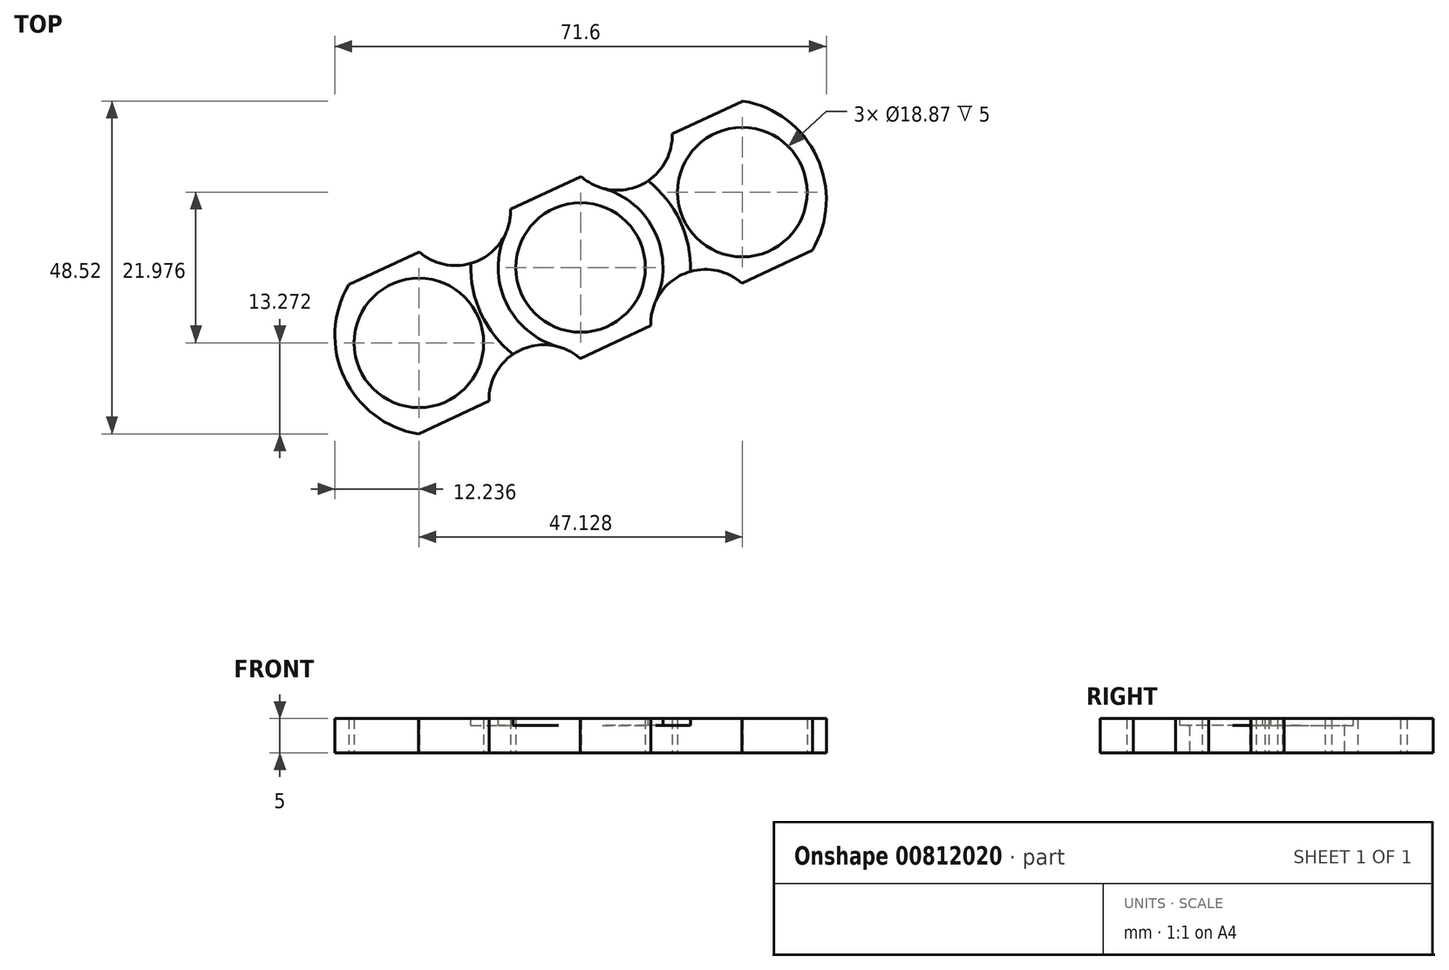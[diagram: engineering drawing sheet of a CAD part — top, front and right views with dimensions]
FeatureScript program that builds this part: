
annotation { "Feature Type Name" : "Feature", "Feature Type Description" : "" }
export const myFeature = defineFeature(function(context is Context, id is Id, definition is map)
    precondition{}
    {
        {
            var Q0;
            Q0=qCreatedBy(makeId("Top.planeOp"),FACE);
            var sketch = newSketch(context, id + "F0", { "sketchPlane" : qUnion([Q0])});
            skCircle(sketch, "E0", {"center": v(0, 0) * mm, "radius": 9.44 * mm});
            skCircle(sketch, "E1", {"center": v(23.56, 10.99) * mm, "radius": 9.44 * mm});
            skCircle(sketch, "E2", {"center": v(-23.56, -10.99) * mm, "radius": 9.44 * mm});
            skLineSegment(sketch, "E3.bottom", {"start": v(-36.75, 25) * mm, "end": v(36.75, 25) * mm, "construction": true});
            skLineSegment(sketch, "E3.top", {"start": v(-36.75, -25) * mm, "end": v(36.75, -25) * mm, "construction": true});
            skLineSegment(sketch, "E3.left", {"start": v(-36.75, 25) * mm, "end": v(-36.75, -25) * mm, "construction": true});
            skLineSegment(sketch, "E3.right", {"start": v(36.75, 25) * mm, "end": v(36.75, -25) * mm, "construction": true});
            skLineSegment(sketch, "E4", {"start": v(-23.56, -10.99) * mm, "end": v(23.56, 10.99) * mm, "construction": true});
            skLineSegment(sketch, "E5", {"start": v(-5.81, 12.46) * mm, "end": v(6.83, -14.65) * mm, "construction": true});
            skLineSegment(sketch, "E6", {"start": v(-33.77, -2.5) * mm, "end": v(-23.5, 2.28) * mm});
            skLineSegment(sketch, "E7", {"start": v(13.36, 19.47) * mm, "end": v(23.63, 24.26) * mm});
            skLineSegment(sketch, "E8", {"start": v(-10.2, 8.48) * mm, "end": v(0.06, 13.27) * mm});
            skLineSegment(sketch, "E9", {"start": v(23.5, -2.28) * mm, "end": v(33.77, 2.5) * mm});
            skLineSegment(sketch, "E10", {"start": v(-23.63, -24.26) * mm, "end": v(-13.36, -19.47) * mm});
            skLineSegment(sketch, "E11", {"start": v(-0.06, -13.27) * mm, "end": v(10.2, -8.48) * mm});
            skArc(sketch, "E12", {"start": v(-33.77, -2.5) * mm, "mid": v(-34.44, -16.06) * mm, "end": v(-23.63, -24.26) * mm});
            skArc(sketch, "E13", {"start": v(33.77, 2.5) * mm, "mid": v(34.44, 16.06) * mm, "end": v(23.63, 24.26) * mm});
            skArc(sketch, "E14", {"start": v(0.06, 13.27) * mm, "mid": v(8.74, 12.02) * mm, "end": v(13.36, 19.47) * mm});
            skArc(sketch, "E15", {"start": v(23.5, -2.28) * mm, "mid": v(14.82, -1.03) * mm, "end": v(10.2, -8.48) * mm});
            skArc(sketch, "E16", {"start": v(-0.06, -13.27) * mm, "mid": v(-8.74, -12.02) * mm, "end": v(-13.36, -19.47) * mm});
            skArc(sketch, "E17", {"start": v(-23.5, 2.28) * mm, "mid": v(-14.82, 1.03) * mm, "end": v(-10.2, 8.48) * mm});
            skLineSegment(sketch, "E18", {"start": v(-23.56, -10.99) * mm, "end": v(-31.51, 6.06) * mm, "construction": true});
            skLineSegment(sketch, "E19", {"start": v(23.56, 10.99) * mm, "end": v(14.6, 30.23) * mm, "construction": true});
            skCircle(sketch, "E20", {"center": v(-23.56, -10.99) * mm, "radius": 12 * mm, "construction": true});
            skCircle(sketch, "E21", {"center": v(0, 0) * mm, "radius": 12 * mm, "construction": true});
            skCircle(sketch, "E22", {"center": v(23.56, 10.99) * mm, "radius": 12 * mm, "construction": true});
            skSolve(sketch);
        }
        {
            var Q0;
            Q0=makeQuery(id+"F0.imprint","IMPRINT",FACE,{"disambiguationData":[TD([[makeQuery(id+"F0.imprint","IMPRINT",EDGE,{"derivedFrom":sQuery(id+"F0.wireOp",EDGE,"E0")}),-1.0]])]});
            extrude(context, id + "F1", {"entities" : qUnion([Q0]), "depth" : 2.5 * mm, "offsetDistance" : 25 * mm, "hasSecondDirection" : true, "secondDirectionOppositeDirection" : true, "secondDirectionDepth" : 2.5 * mm});
        }
        {
            var Q0;
            Q0=makeQuery(id+"F1.opExtrude","CAP_FACE",FACE,{"disambiguationData":[OSD([sQuery(id+"F0.wireOp",EDGE,"E0"),sQuery(id+"F0.wireOp",EDGE,"E1"),sQuery(id+"F0.wireOp",EDGE,"E2"),sQuery(id+"F0.wireOp",EDGE,"E6"),sQuery(id+"F0.wireOp",EDGE,"E7"),sQuery(id+"F0.wireOp",EDGE,"E8"),sQuery(id+"F0.wireOp",EDGE,"E9"),sQuery(id+"F0.wireOp",EDGE,"E10"),sQuery(id+"F0.wireOp",EDGE,"E11"),sQuery(id+"F0.wireOp",EDGE,"E12"),sQuery(id+"F0.wireOp",EDGE,"E13"),sQuery(id+"F0.wireOp",EDGE,"E14"),sQuery(id+"F0.wireOp",EDGE,"E15"),sQuery(id+"F0.wireOp",EDGE,"E16"),sQuery(id+"F0.wireOp",EDGE,"E17")])],"isStart":false});
            var sketch = newSketch(context, id + "F2", { "sketchPlane" : qUnion([Q0])});
            skCircle(sketch, "E23", {"center": v(0, 0) * mm, "radius": 12 * mm});
            skCircle(sketch, "E24", {"center": v(0, 0) * mm, "radius": 16 * mm});
            skSolve(sketch);
        }
        {
            var Q0;
            Q0=makeQuery(id+"F2.imprint","IMPRINT",FACE,{"disambiguationData":[TD([[makeQuery(id+"F2.imprint","IMPRINT",EDGE,{"derivedFrom":makeQuery(id+"F1.opExtrude","CAP_EDGE",EDGE,{"disambiguationData":[OSD([sQuery(id+"F0.wireOp",EDGE,"E0")])],"isStart":false})}),1.0]])]});
            var Q1;
            Q1=makeQuery(id+"F2.imprint","IMPRINT",FACE,{"disambiguationData":[TD([[makeQuery(id+"F2.imprint","IMPRINT",EDGE,{"derivedFrom":makeQuery(id+"F1.opExtrude","CAP_EDGE",EDGE,{"disambiguationData":[OSD([sQuery(id+"F0.wireOp",EDGE,"E1")])],"isStart":false})}),1.0]])]});
            var Q2;
            Q2=makeQuery(id+"F2.imprint","IMPRINT",FACE,{"disambiguationData":[TD([[makeQuery(id+"F2.imprint","IMPRINT",EDGE,{"derivedFrom":makeQuery(id+"F1.opExtrude","CAP_EDGE",EDGE,{"disambiguationData":[OSD([sQuery(id+"F0.wireOp",EDGE,"E2")])],"isStart":false})}),1.0]])]});
            var Q3;
            {var subQ0=sQuery(id+"F2.wireOp",EDGE,"FtA3bayP-j3OT-VSZs-aEoY-GLu4wzKhFJMj");var subQ1=makeQuery(id+"F1.opExtrude","CAP_EDGE",EDGE,{"disambiguationData":[OSD([sQuery(id+"F0.wireOp",EDGE,"E6")])],"isStart":false});var subQ2=makeQuery(id+"F2.imprint","INTERSECT",VERTEX,{"derivedFrom":[subQ1,subQ0]});Q3=makeQuery(id+"F2.imprint","IMPRINT",FACE,{"disambiguationData":[TD([[makeQuery(id+"F2.imprint","IMPRINT",EDGE,{"disambiguationData":[TD([[subQ2,1.0]])],"derivedFrom":subQ0}),-1.0]])]});}
            var Q4;
            {var subQ0=sQuery(id+"F2.wireOp",EDGE,"E23");var subQ1=makeQuery(id+"F1.opExtrude","CAP_EDGE",EDGE,{"disambiguationData":[OSD([sQuery(id+"F0.wireOp",EDGE,"E17")])],"isStart":false});var subQ2=makeQuery(id+"F2.imprint","INTERSECT",VERTEX,{"derivedFrom":[subQ1,subQ0]});Q4=makeQuery(id+"F2.imprint","IMPRINT",FACE,{"disambiguationData":[TD([[makeQuery(id+"F2.imprint","IMPRINT",EDGE,{"disambiguationData":[TD([[subQ2,-1.0]])],"derivedFrom":subQ0}),-1.0]])]});}
            var Q5;
            {var subQ0=sQuery(id+"F2.wireOp",EDGE,"t8nWiPke-CIwg-3ZqW-WhvU-Z3H4iyrQB45r");var subQ1=makeQuery(id+"F1.opExtrude","CAP_EDGE",EDGE,{"disambiguationData":[OSD([sQuery(id+"F0.wireOp",EDGE,"E14")])],"isStart":false});var subQ2=makeQuery(id+"F2.imprint","INTERSECT",VERTEX,{"derivedFrom":[subQ1,subQ0]});Q5=makeQuery(id+"F2.imprint","IMPRINT",FACE,{"disambiguationData":[TD([[makeQuery(id+"F2.imprint","IMPRINT",EDGE,{"disambiguationData":[TD([[subQ2,-1.0]])],"derivedFrom":subQ0}),-1.0]])]});}
            var Q6;
            {var subQ0=sQuery(id+"F2.wireOp",EDGE,"t8nWiPke-CIwg-3ZqW-WhvU-Z3H4iyrQB45r");var subQ1=makeQuery(id+"F1.opExtrude","CAP_EDGE",EDGE,{"disambiguationData":[OSD([sQuery(id+"F0.wireOp",EDGE,"E15")])],"isStart":false});var subQ2=makeQuery(id+"F2.imprint","INTERSECT",VERTEX,{"derivedFrom":[subQ1,subQ0]});Q6=makeQuery(id+"F2.imprint","IMPRINT",FACE,{"disambiguationData":[TD([[makeQuery(id+"F2.imprint","IMPRINT",EDGE,{"disambiguationData":[TD([[subQ2,-1.0]])],"derivedFrom":subQ0}),-1.0]])]});}
            var Q7;
            {var subQ0=sQuery(id+"F2.wireOp",EDGE,"t8nWiPke-CIwg-3ZqW-WhvU-Z3H4iyrQB45r");var subQ1=makeQuery(id+"F1.opExtrude","CAP_EDGE",EDGE,{"disambiguationData":[OSD([sQuery(id+"F0.wireOp",EDGE,"E13")])],"isStart":false});var subQ2=makeQuery(id+"F2.imprint","INTERSECT",VERTEX,{"derivedFrom":[subQ1,subQ0]});Q7=makeQuery(id+"F2.imprint","IMPRINT",FACE,{"disambiguationData":[TD([[makeQuery(id+"F2.imprint","IMPRINT",EDGE,{"disambiguationData":[TD([[subQ2,1.0]])],"derivedFrom":subQ0}),-1.0]])]});}
            var Q8;
            {var subQ0=sQuery(id+"F2.wireOp",EDGE,"t8nWiPke-CIwg-3ZqW-WhvU-Z3H4iyrQB45r");var subQ1=makeQuery(id+"F1.opExtrude","CAP_EDGE",EDGE,{"disambiguationData":[OSD([sQuery(id+"F0.wireOp",EDGE,"E7")])],"isStart":false});var subQ2=makeQuery(id+"F2.imprint","INTERSECT",VERTEX,{"derivedFrom":[subQ1,subQ0]});Q8=makeQuery(id+"F2.imprint","IMPRINT",FACE,{"disambiguationData":[TD([[makeQuery(id+"F2.imprint","IMPRINT",EDGE,{"disambiguationData":[TD([[subQ2,1.0]])],"derivedFrom":subQ0}),-1.0]])]});}
            var Q9;
            {var subQ0=sQuery(id+"F2.wireOp",EDGE,"t8nWiPke-CIwg-3ZqW-WhvU-Z3H4iyrQB45r");var subQ1=makeQuery(id+"F1.opExtrude","CAP_EDGE",EDGE,{"disambiguationData":[OSD([sQuery(id+"F0.wireOp",EDGE,"E7")])],"isStart":false});var subQ2=makeQuery(id+"F2.imprint","INTERSECT",VERTEX,{"derivedFrom":[subQ1,subQ0]});Q9=makeQuery(id+"F2.imprint","IMPRINT",FACE,{"disambiguationData":[TD([[makeQuery(id+"F2.imprint","IMPRINT",EDGE,{"disambiguationData":[TD([[subQ2,-1.0]])],"derivedFrom":subQ0}),-1.0]])]});}
            var Q10;
            {var subQ0=sQuery(id+"F2.wireOp",EDGE,"FtA3bayP-j3OT-VSZs-aEoY-GLu4wzKhFJMj");var subQ1=makeQuery(id+"F1.opExtrude","CAP_EDGE",EDGE,{"disambiguationData":[OSD([sQuery(id+"F0.wireOp",EDGE,"E6")])],"isStart":false});var subQ2=makeQuery(id+"F2.imprint","INTERSECT",VERTEX,{"derivedFrom":[subQ1,subQ0]});Q10=makeQuery(id+"F2.imprint","IMPRINT",FACE,{"disambiguationData":[TD([[makeQuery(id+"F2.imprint","IMPRINT",EDGE,{"disambiguationData":[TD([[subQ2,-1.0]])],"derivedFrom":subQ0}),-1.0]])]});}
            var Q11;
            {var subQ0=sQuery(id+"F2.wireOp",EDGE,"FtA3bayP-j3OT-VSZs-aEoY-GLu4wzKhFJMj");var subQ1=makeQuery(id+"F1.opExtrude","CAP_EDGE",EDGE,{"disambiguationData":[OSD([sQuery(id+"F0.wireOp",EDGE,"E12")])],"isStart":false});var subQ2=makeQuery(id+"F2.imprint","INTERSECT",VERTEX,{"derivedFrom":[subQ1,subQ0]});Q11=makeQuery(id+"F2.imprint","IMPRINT",FACE,{"disambiguationData":[TD([[makeQuery(id+"F2.imprint","IMPRINT",EDGE,{"disambiguationData":[TD([[subQ2,-1.0]])],"derivedFrom":subQ0}),-1.0]])]});}
            var Q12;
            {var subQ0=sQuery(id+"F2.wireOp",EDGE,"FtA3bayP-j3OT-VSZs-aEoY-GLu4wzKhFJMj");var subQ1=makeQuery(id+"F1.opExtrude","CAP_EDGE",EDGE,{"disambiguationData":[OSD([sQuery(id+"F0.wireOp",EDGE,"E10")])],"isStart":false});var subQ2=makeQuery(id+"F2.imprint","INTERSECT",VERTEX,{"derivedFrom":[subQ1,subQ0]});Q12=makeQuery(id+"F2.imprint","IMPRINT",FACE,{"disambiguationData":[TD([[makeQuery(id+"F2.imprint","IMPRINT",EDGE,{"disambiguationData":[TD([[subQ2,-1.0]])],"derivedFrom":subQ0}),-1.0]])]});}
            var Q13;
            {var subQ0=sQuery(id+"F2.wireOp",EDGE,"E23");var subQ1=makeQuery(id+"F1.opExtrude","CAP_EDGE",EDGE,{"disambiguationData":[OSD([sQuery(id+"F0.wireOp",EDGE,"E14")])],"isStart":false});var subQ2=makeQuery(id+"F2.imprint","INTERSECT",VERTEX,{"derivedFrom":[subQ1,subQ0]});Q13=makeQuery(id+"F2.imprint","IMPRINT",FACE,{"disambiguationData":[TD([[makeQuery(id+"F2.imprint","IMPRINT",EDGE,{"disambiguationData":[TD([[subQ2,1.0]])],"derivedFrom":subQ0}),-1.0]])]});}
            extrude(context, id + "F3", {"entities" : qUnion([Q0, Q1, Q2, Q3, Q4, Q5, Q6, Q7, Q8, Q9, Q10, Q11, Q12, Q13]), "operationType" : NewBodyOperationType.REMOVE, "oppositeDirection" : true, "depth" : 1 * mm, "offsetDistance" : 25 * mm});
        }
    });
